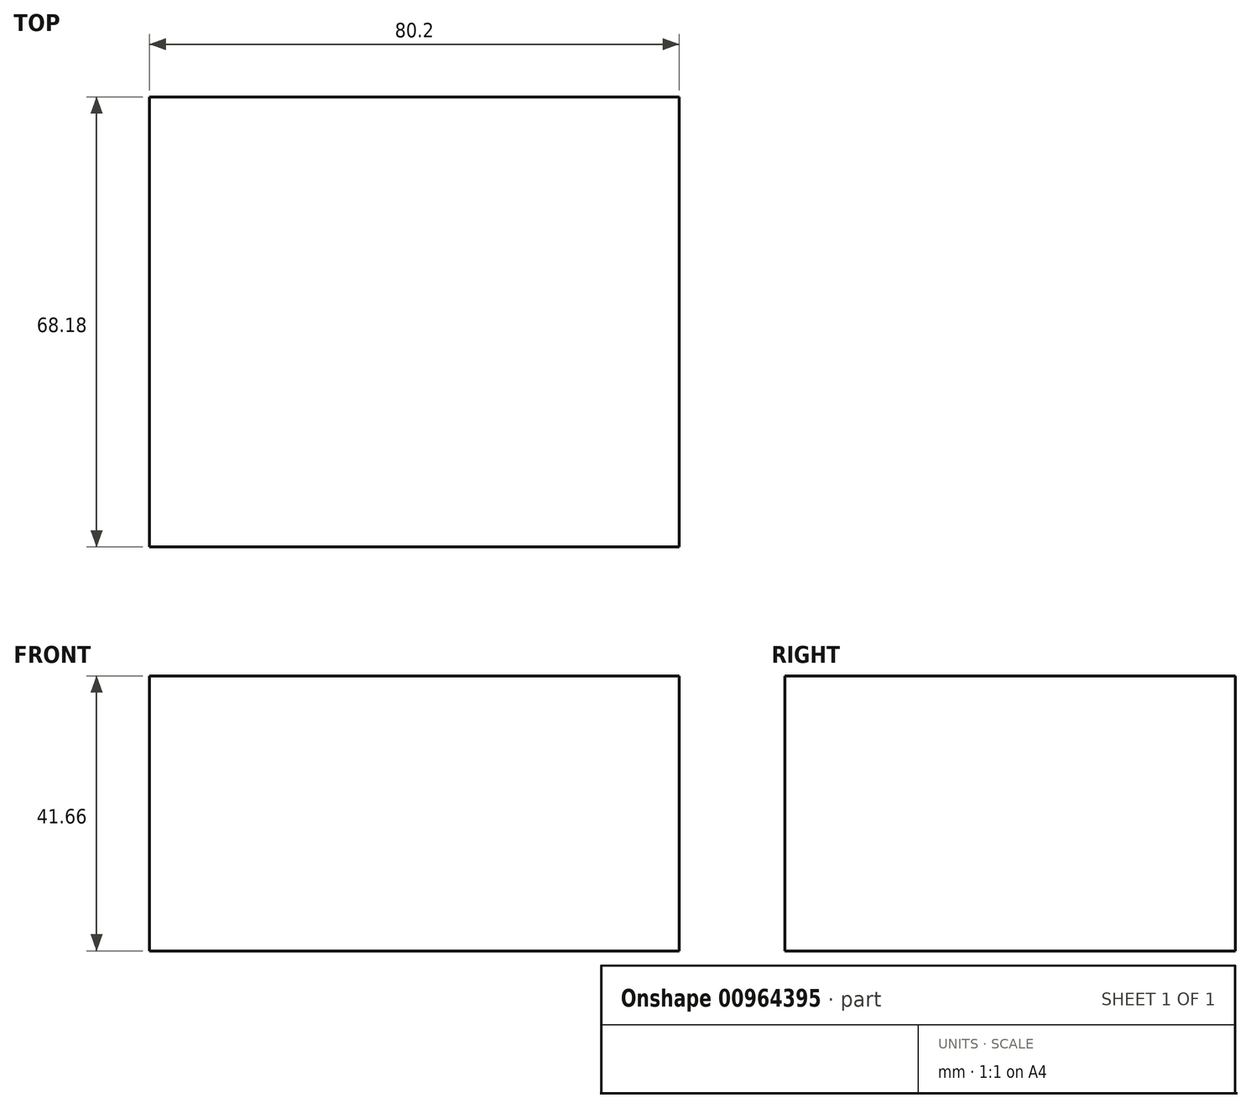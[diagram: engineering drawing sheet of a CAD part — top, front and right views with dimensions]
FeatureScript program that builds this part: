
annotation { "Feature Type Name" : "Feature", "Feature Type Description" : "" }
export const myFeature = defineFeature(function(context is Context, id is Id, definition is map)
    precondition{}
    {
        {
            var Q0;
            Q0=qCreatedBy(makeId("Top.planeOp"),FACE);
            var sketch = newSketch(context, id + "F0", { "sketchPlane" : qUnion([Q0])});
            skLineSegment(sketch, "E0.bottom", {"start": v(-45.84, 0) * mm, "end": v(34.36, 0) * mm});
            skLineSegment(sketch, "E0.top", {"start": v(-45.84, 68.18) * mm, "end": v(34.36, 68.18) * mm});
            skLineSegment(sketch, "E0.left", {"start": v(-45.84, 0) * mm, "end": v(-45.84, 68.18) * mm});
            skLineSegment(sketch, "E0.right", {"start": v(34.36, 0) * mm, "end": v(34.36, 68.18) * mm});
            skSolve(sketch);
        }
        {
            var Q0;
            Q0=makeQuery(id+"F0.imprint","IMPRINT",FACE,{"disambiguationData":[TD([[makeQuery(id+"F0.imprint","IMPRINT",EDGE,{"derivedFrom":sQuery(id+"F0.wireOp",EDGE,"E0.bottom")}),1.0]])]});
            extrude(context, id + "F1", {"entities" : qUnion([Q0]), "depth" : 41.66 * mm, "offsetDistance" : 25.4 * mm});
        }
    });
